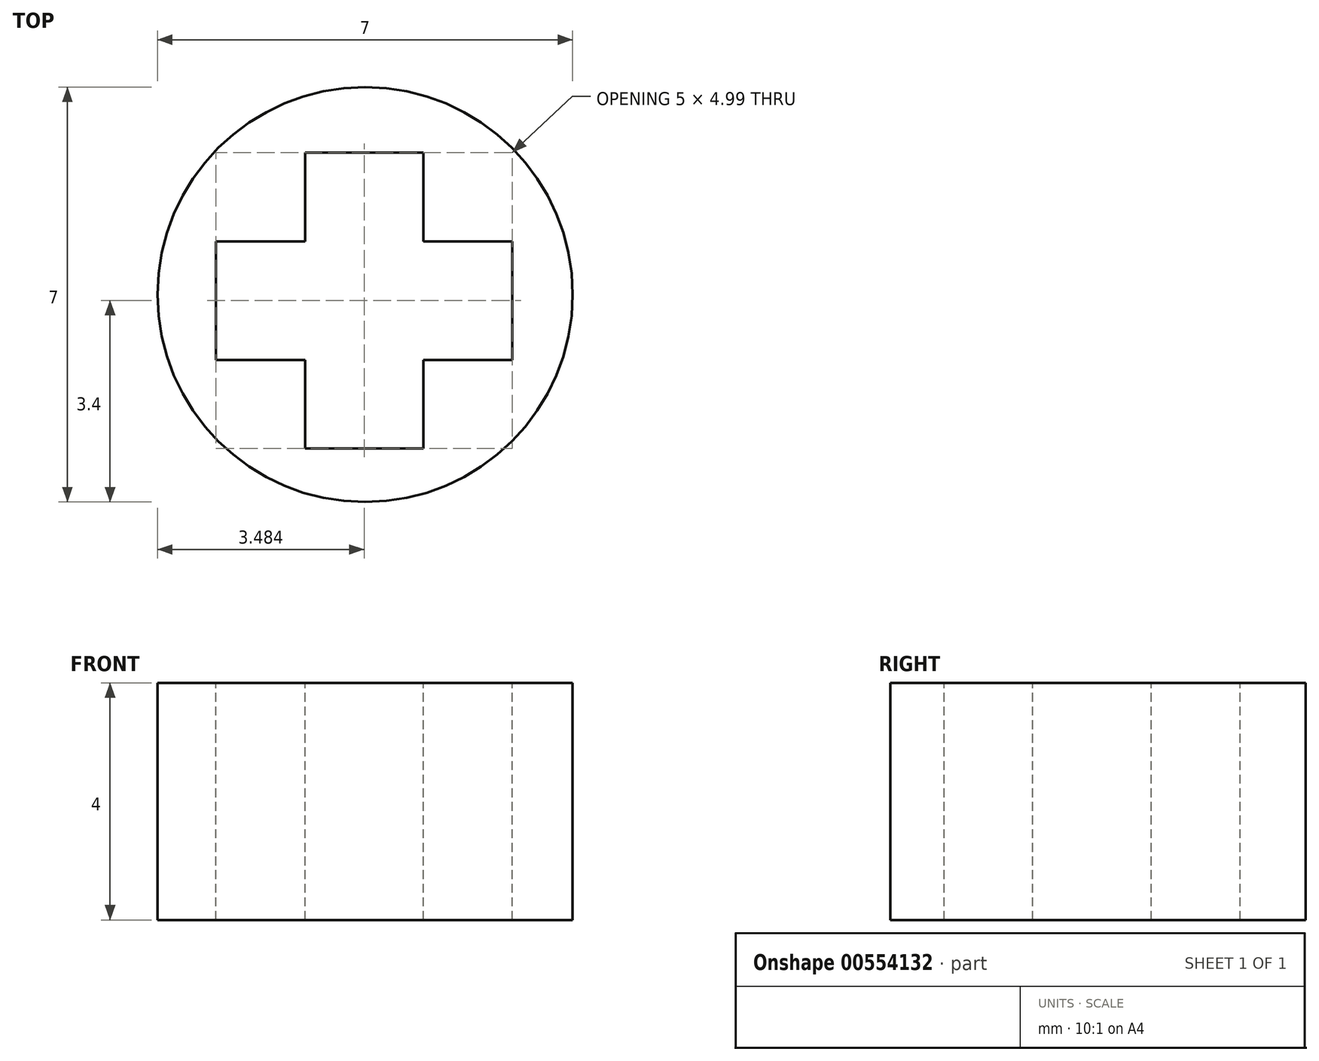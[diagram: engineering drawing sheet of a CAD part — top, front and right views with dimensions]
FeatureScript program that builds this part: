
annotation { "Feature Type Name" : "Feature", "Feature Type Description" : "" }
export const myFeature = defineFeature(function(context is Context, id is Id, definition is map)
    precondition{}
    {
        {
            var Q0;
            Q0=qCreatedBy(makeId("Top.planeOp"),FACE);
            var sketch = newSketch(context, id + "F0", { "sketchPlane" : qUnion([Q0])});
            skCircle(sketch, "E0", {"center": v(0, 0) * mm, "radius": 3.5 * mm});
            skSolve(sketch);
        }
        {
            var Q0;
            Q0=makeQuery(id+"F0.imprint","IMPRINT",FACE,{"disambiguationData":[TD([[makeQuery(id+"F0.imprint","IMPRINT",EDGE,{"derivedFrom":sQuery(id+"F0.wireOp",EDGE,"E0")}),1.0]])]});
            extrude(context, id + "F1", {"entities" : qUnion([Q0]), "depth" : 4 * mm, "offsetDistance" : 25.4 * mm});
        }
        {
            var Q0;
            Q0=makeQuery(id+"F1.opExtrude","CAP_FACE",FACE,{"disambiguationData":[OSD([sQuery(id+"F0.wireOp",EDGE,"E0")])],"isStart":false});
            var sketch = newSketch(context, id + "F2", { "sketchPlane" : qUnion([Q0])});
            skLineSegment(sketch, "E1", {"start": v(0.98, -2.6) * mm, "end": v(0, -2.6) * mm});
            skLineSegment(sketch, "E2", {"start": v(0, -2.6) * mm, "end": v(-1.01, -2.6) * mm});
            skLineSegment(sketch, "E3", {"start": v(-1.01, -2.6) * mm, "end": v(-1.01, -1.1) * mm});
            skLineSegment(sketch, "E4", {"start": v(0.98, -2.6) * mm, "end": v(0.98, -1.1) * mm});
            skLineSegment(sketch, "E5", {"start": v(0.98, -1.1) * mm, "end": v(2.48, -1.1) * mm});
            skLineSegment(sketch, "E6", {"start": v(-1.01, -1.1) * mm, "end": v(-2.51, -1.1) * mm});
            skLineSegment(sketch, "E7", {"start": v(-2.51, -1.1) * mm, "end": v(-2.51, 0.9) * mm});
            skLineSegment(sketch, "E8", {"start": v(2.48, -1.1) * mm, "end": v(2.48, 0.9) * mm});
            skLineSegment(sketch, "E9", {"start": v(-2.51, 0.9) * mm, "end": v(-1.01, 0.9) * mm});
            skLineSegment(sketch, "E10", {"start": v(2.48, 0.9) * mm, "end": v(0.98, 0.9) * mm});
            skLineSegment(sketch, "E11", {"start": v(-1.01, 0.9) * mm, "end": v(-1.01, 2.4) * mm});
            skLineSegment(sketch, "E12", {"start": v(0.98, 0.9) * mm, "end": v(0.98, 2.4) * mm});
            skLineSegment(sketch, "E13", {"start": v(0.98, 2.4) * mm, "end": v(-1.01, 2.4) * mm});
            skSolve(sketch);
        }
        {
            var Q0;
            Q0 = qSketchRegion(id + "F2", true);
            extrude(context, id + "F3", {"entities" : qUnion([Q0]), "operationType" : NewBodyOperationType.REMOVE, "oppositeDirection" : true, "depth" : 4 * mm, "offsetDistance" : 25.4 * mm});
        }
    });
